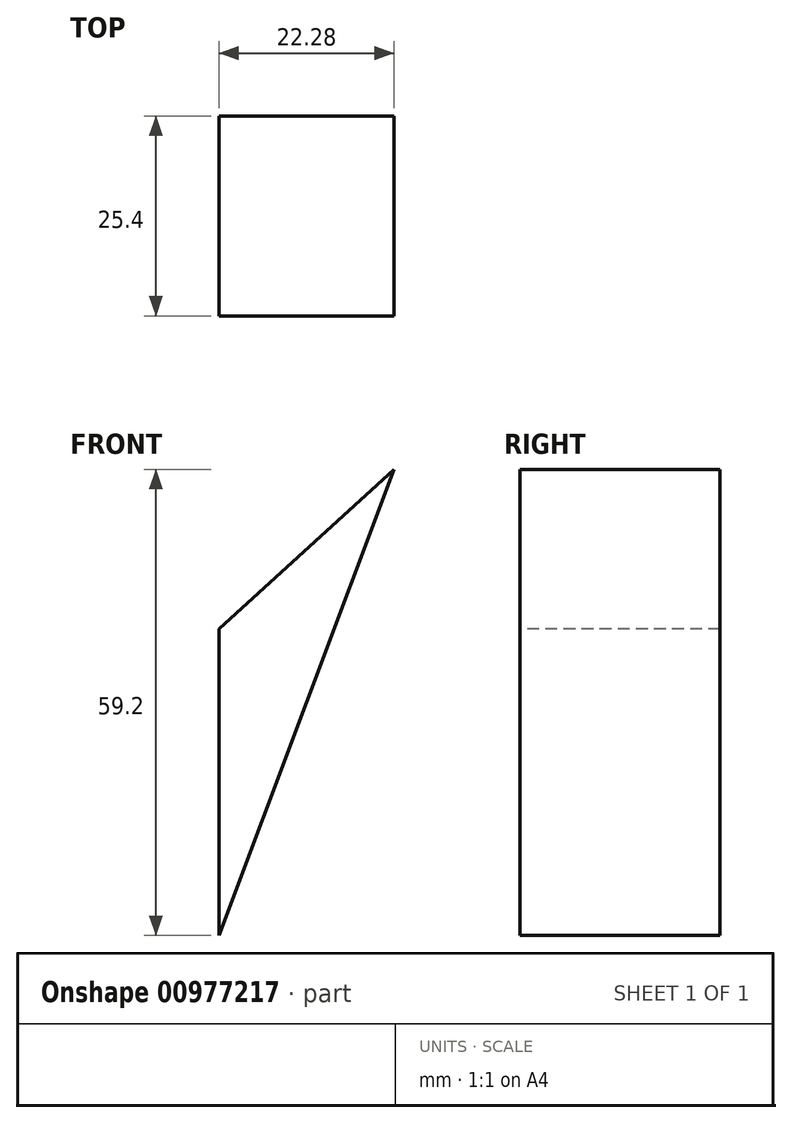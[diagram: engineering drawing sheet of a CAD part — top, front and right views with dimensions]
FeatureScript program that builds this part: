
annotation { "Feature Type Name" : "Feature", "Feature Type Description" : "" }
export const myFeature = defineFeature(function(context is Context, id is Id, definition is map)
    precondition{}
    {
        {
            var Q0;
            Q0=qCreatedBy(makeId("Front.planeOp"),FACE);
            var sketch = newSketch(context, id + "F0", { "sketchPlane" : qUnion([Q0])});
            skLineSegment(sketch, "E0", {"start": v(87.27, 83.74) * mm, "end": v(65, 63.49) * mm});
            skLineSegment(sketch, "E1", {"start": v(65, 63.49) * mm, "end": v(65, 24.54) * mm});
            skLineSegment(sketch, "E2", {"start": v(65, 24.54) * mm, "end": v(87.27, 83.74) * mm});
            skSolve(sketch);
        }
        {
            var Q0;
            Q0=sQuery(id+"F0.wireOp",EDGE,"E1");
            var Q1;
            Q1=sQuery(id+"F0.wireOp",EDGE,"E2");
            var Q2;
            Q2=sQuery(id+"F0.wireOp",EDGE,"E0");
            extrude(context, id + "F1", {"bodyType" : ToolBodyType.SURFACE, "surfaceEntities" : qUnion([Q0, Q1, Q2]), "depth" : 25.4 * mm, "offsetDistance" : 25.4 * mm});
        }
    });
